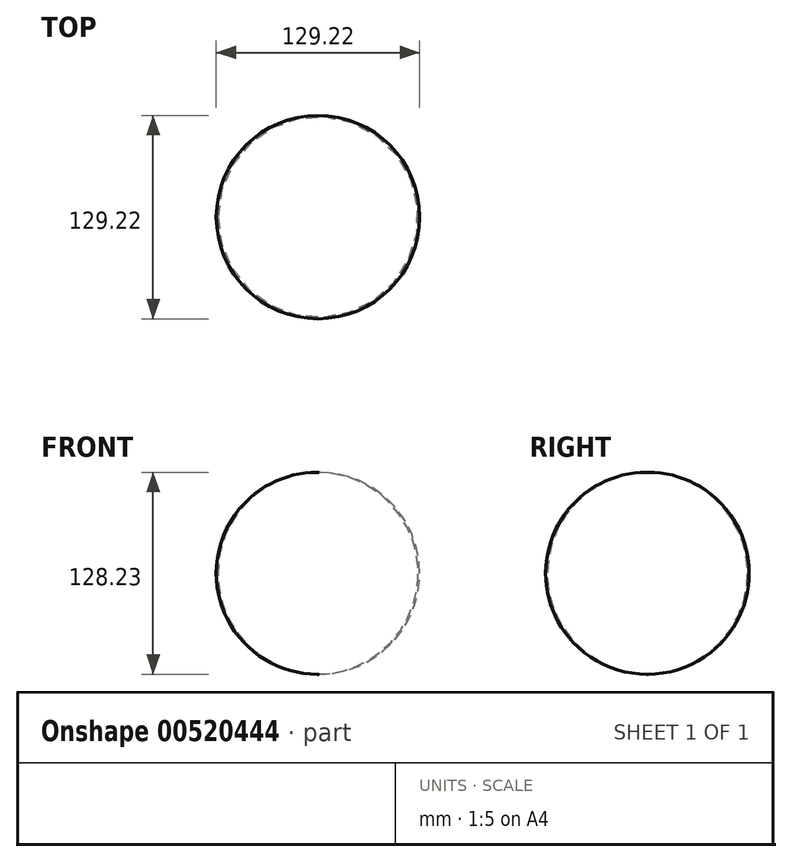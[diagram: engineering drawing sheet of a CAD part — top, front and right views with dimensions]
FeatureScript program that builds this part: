
annotation { "Feature Type Name" : "Feature", "Feature Type Description" : "" }
export const myFeature = defineFeature(function(context is Context, id is Id, definition is map)
    precondition{}
    {
        {
            var Q0;
            Q0=qCreatedBy(makeId("Front.planeOp"),FACE);
            var sketch = newSketch(context, id + "F0", { "sketchPlane" : qUnion([Q0])});
            skLineSegment(sketch, "E0", {"start": v(0, 74.83) * mm, "end": v(0, -75.98) * mm});
            skArc(sketch, "E1", {"start": v(0, 56.7) * mm, "mid": v(-63.62, -7.41) * mm, "end": v(0, -71.53) * mm});
            skPoint(sketch, "E2.orphan", {"position": v(64.18, 0) * mm});
            skSolve(sketch);
        }
        {
            var Q0;
            {var subQ0=sQuery(id+"F0.wireOp",EDGE,"E1");Q0=makeQuery(id+"F0.imprint","IMPRINT",FACE,{"disambiguationData":[TD([[makeQuery(id+"F0.imprint","IMPRINT",EDGE,{"derivedFrom":subQ0}),1.0]])]});}
            var Q1;
            Q1=sQuery(id+"F0.wireOp",EDGE,"E0");
            revolve(context, id + "F1", {"entities" : qUnion([Q0]), "axis" : qUnion([Q1]), "revolveType" : RevolveType.FULL});
        }
    });
